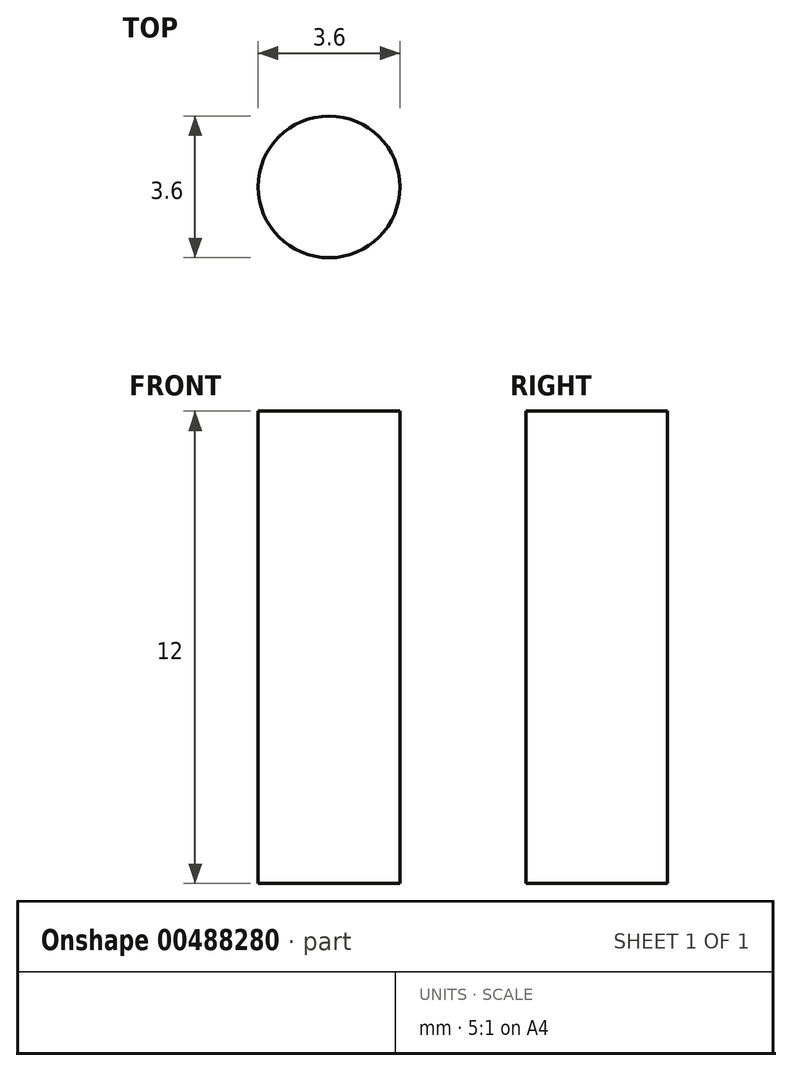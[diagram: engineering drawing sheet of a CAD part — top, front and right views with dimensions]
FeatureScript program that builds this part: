
annotation { "Feature Type Name" : "Feature", "Feature Type Description" : "" }
export const myFeature = defineFeature(function(context is Context, id is Id, definition is map)
    precondition{}
    {
        {
            var Q0;
            Q0=qCreatedBy(makeId("Top.planeOp"),FACE);
            var sketch = newSketch(context, id + "F0", { "sketchPlane" : qUnion([Q0])});
            skCircle(sketch, "E0", {"center": v(0, 0) * mm, "radius": 1.8 * mm});
            skSolve(sketch);
        }
        {
            var Q0;
            Q0 = qSketchRegion(id + "F0", true);
            extrude(context, id + "F1", {"entities" : qUnion([Q0]), "endBound" : BoundingType.SYMMETRIC, "depth" : 12 * mm});
        }
    });
